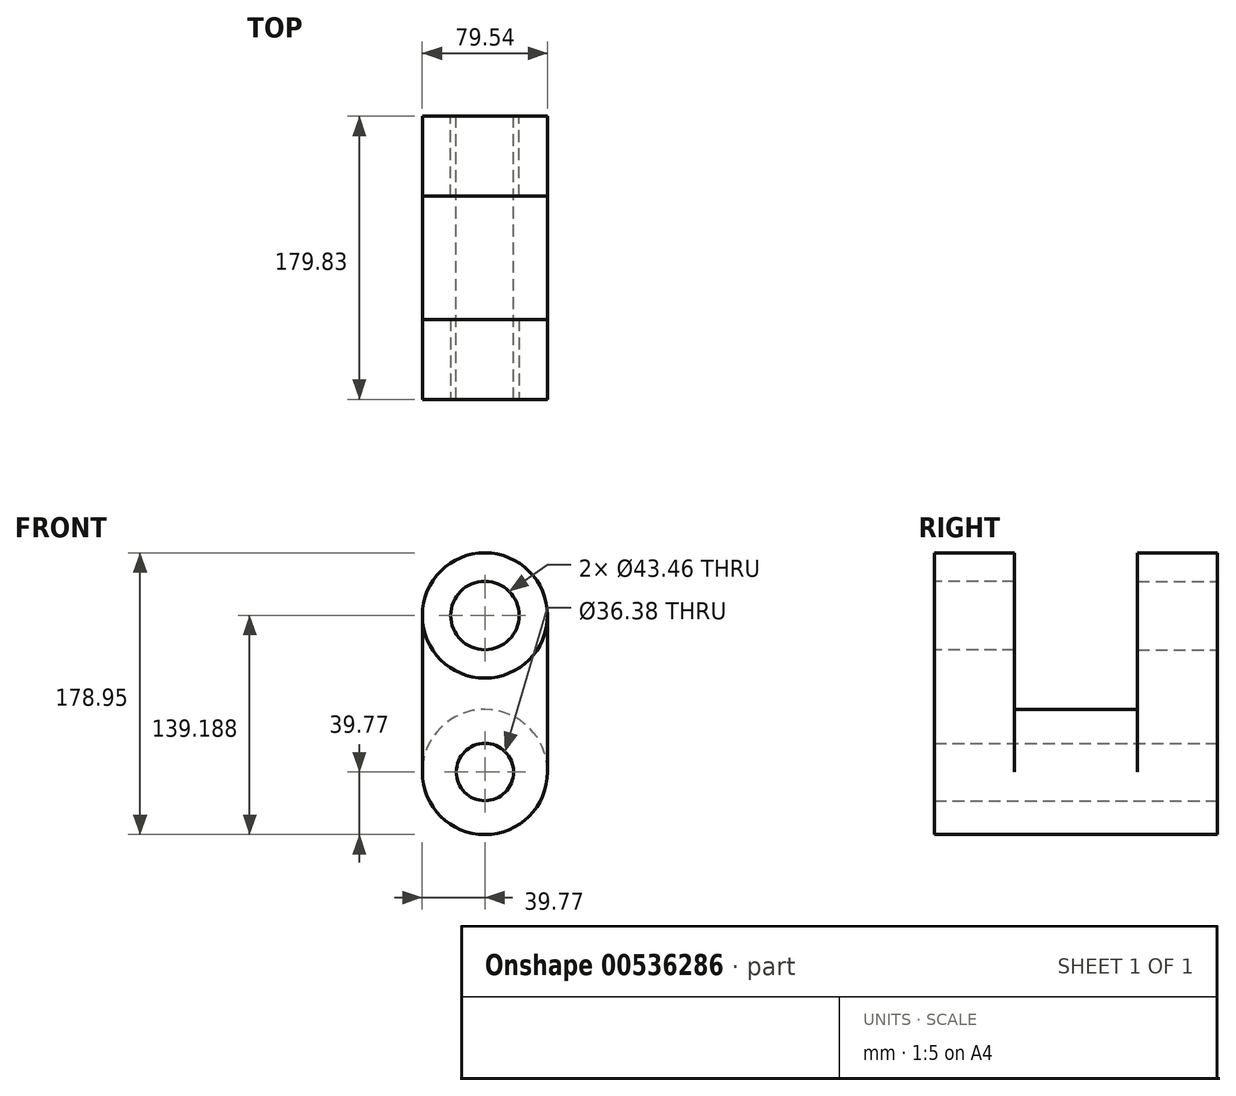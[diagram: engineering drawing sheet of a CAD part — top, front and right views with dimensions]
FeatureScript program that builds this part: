
annotation { "Feature Type Name" : "Feature", "Feature Type Description" : "" }
export const myFeature = defineFeature(function(context is Context, id is Id, definition is map)
    precondition{}
    {
        {
            var Q0;
            Q0=qCreatedBy(makeId("Front.planeOp"),FACE);
            var sketch = newSketch(context, id + "F0", { "sketchPlane" : qUnion([Q0])});
            skCircle(sketch, "E0", {"center": v(0, 0) * mm, "radius": 39.77 * mm});
            skCircle(sketch, "E1", {"center": v(0, 0) * mm, "radius": 18.2 * mm});
            skSolve(sketch);
        }
        {
            var Q0;
            Q0 = qSketchRegion(id + "F0", true);
            extrude(context, id + "F1", {"entities" : qUnion([Q0]), "depth" : 179.83 * mm, "offsetDistance" : 25.4 * mm});
        }
        {
            var Q0;
            Q0=makeQuery(id+"F1.opExtrude","CAP_FACE",FACE,{"disambiguationData":[OSD([sQuery(id+"F0.wireOp",EDGE,"E0"),sQuery(id+"F0.wireOp",EDGE,"E1")])],"isStart":false});
            var sketch = newSketch(context, id + "F2", { "sketchPlane" : qUnion([Q0])});
            skLineSegment(sketch, "E2", {"start": v(-39.77, 0) * mm, "end": v(-39.77, 99.42) * mm});
            skLineSegment(sketch, "E3", {"start": v(39.77, 0) * mm, "end": v(39.77, 99.42) * mm});
            skLineSegment(sketch, "E4", {"start": v(39.77, 99.42) * mm, "end": v(21.73, 99.42) * mm});
            skArc(sketch, "E5", {"start": v(-39.77, 99.42) * mm, "mid": v(0, 139.18) * mm, "end": v(39.77, 99.42) * mm});
            skCircle(sketch, "E6", {"center": v(0, 99.42) * mm, "radius": 21.73 * mm});
            skLineSegment(sketch, "E7.trimOffspring", {"start": v(-21.73, 99.42) * mm, "end": v(-39.77, 99.42) * mm});
            skSolve(sketch);
        }
        {
            var Q0;
            Q0=makeQuery(id+"F1.opExtrude","CAP_FACE",FACE,{"disambiguationData":[OSD([sQuery(id+"F0.wireOp",EDGE,"E0"),sQuery(id+"F0.wireOp",EDGE,"E1")])],"isStart":true});
            var sketch = newSketch(context, id + "F3", { "sketchPlane" : qUnion([Q0])});
            skLineSegment(sketch, "E8", {"start": v(-39.77, 0) * mm, "end": v(-39.77, 99.42) * mm});
            skLineSegment(sketch, "E9", {"start": v(39.77, 0) * mm, "end": v(39.77, 99.42) * mm});
            skLineSegment(sketch, "E10", {"start": v(-39.77, 99.42) * mm, "end": v(-21.73, 99.42) * mm});
            skArc(sketch, "E11", {"start": v(-39.77, 99.42) * mm, "mid": v(0, 139.18) * mm, "end": v(39.77, 99.42) * mm});
            skCircle(sketch, "E12", {"center": v(0, 99.42) * mm, "radius": 21.73 * mm});
            skLineSegment(sketch, "E13.trimOffspring", {"start": v(21.73, 99.42) * mm, "end": v(39.77, 99.42) * mm});
            skSolve(sketch);
        }
        {
            var Q0;
            {var subQ4=sQuery(id+"F3.wireOp",EDGE,"E8");Q0=makeQuery(id+"F3.imprint","IMPRINT",FACE,{"disambiguationData":[TD([[makeQuery(id+"F3.imprint","IMPRINT",EDGE,{"derivedFrom":subQ4}),-1.0]])]});}
            var Q1;
            {var subQ0=sQuery(id+"F3.wireOp",EDGE,"E10");Q1=makeQuery(id+"F3.imprint","IMPRINT",FACE,{"disambiguationData":[TD([[makeQuery(id+"F3.imprint","IMPRINT",EDGE,{"derivedFrom":subQ0}),1.0]])]});}
            extrude(context, id + "F4", {"entities" : qUnion([Q0, Q1]), "operationType" : NewBodyOperationType.ADD, "oppositeDirection" : true, "depth" : 50.8 * mm, "offsetDistance" : 25.4 * mm});
        }
        {
            var Q0;
            {var subQ4=sQuery(id+"F2.wireOp",EDGE,"E2");Q0=makeQuery(id+"F2.imprint","IMPRINT",FACE,{"disambiguationData":[TD([[makeQuery(id+"F2.imprint","IMPRINT",EDGE,{"derivedFrom":subQ4}),-1.0]])]});}
            var Q1;
            {var subQ0=sQuery(id+"F2.wireOp",EDGE,"E4");Q1=makeQuery(id+"F2.imprint","IMPRINT",FACE,{"disambiguationData":[TD([[makeQuery(id+"F2.imprint","IMPRINT",EDGE,{"derivedFrom":subQ0}),-1.0]])]});}
            extrude(context, id + "F5", {"entities" : qUnion([Q0, Q1]), "operationType" : NewBodyOperationType.ADD, "oppositeDirection" : true, "depth" : 50.8 * mm, "offsetDistance" : 25.4 * mm});
        }
    });
